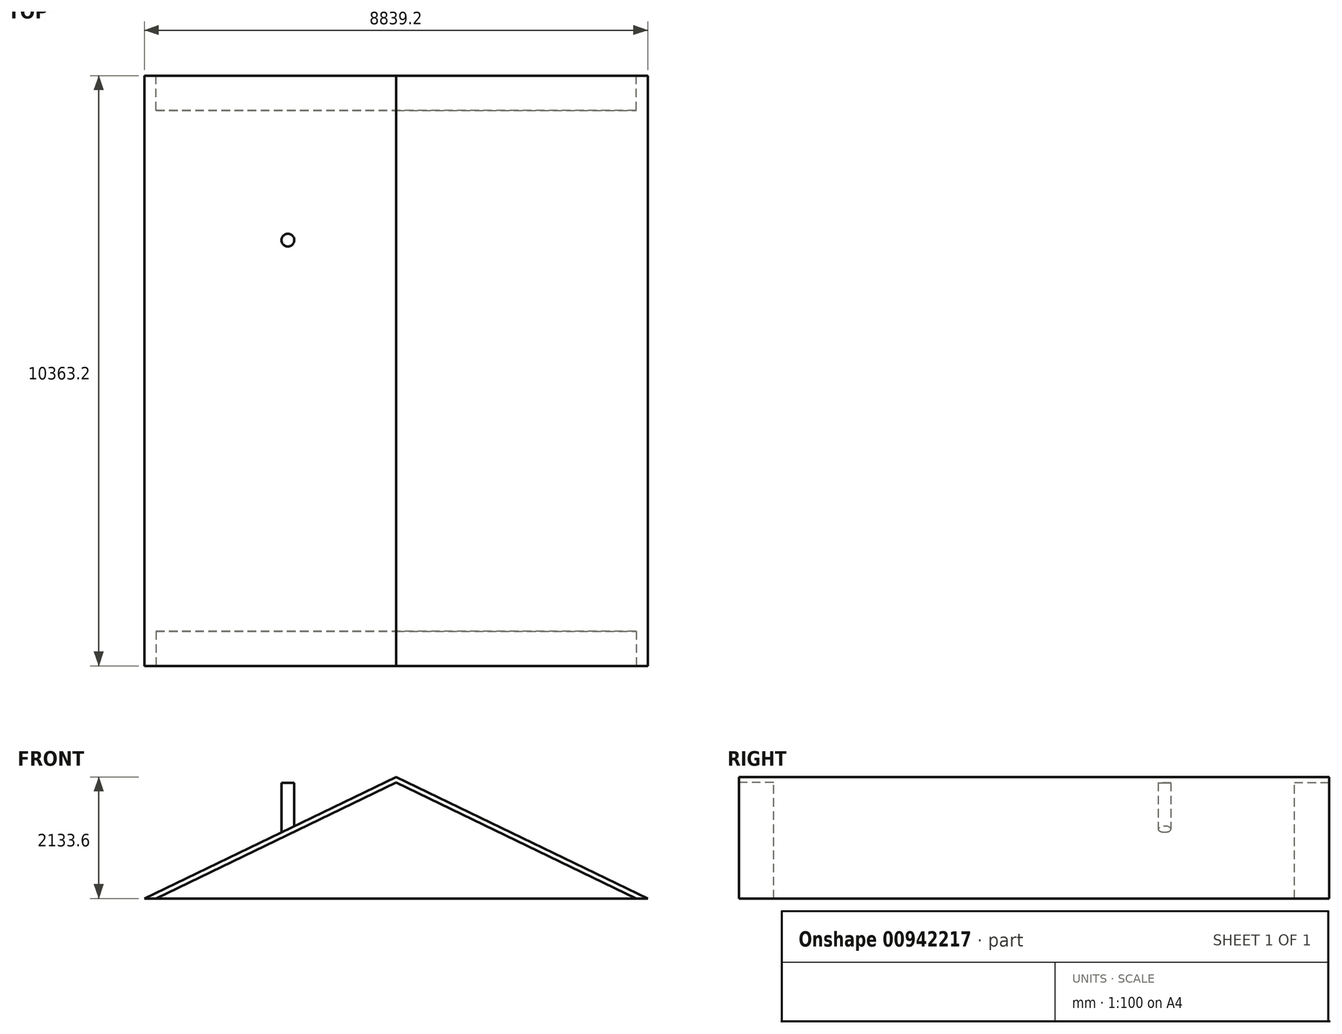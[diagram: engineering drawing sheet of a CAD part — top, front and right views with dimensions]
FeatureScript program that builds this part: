
annotation { "Feature Type Name" : "Feature", "Feature Type Description" : "" }
export const myFeature = defineFeature(function(context is Context, id is Id, definition is map)
    precondition{}
    {
        {
            var Q0;
            Q0=qCreatedBy(makeId("Front.planeOp"),FACE);
            var sketch = newSketch(context, id + "F0", { "sketchPlane" : qUnion([Q0])});
            skLineSegment(sketch, "E0", {"start": v(0, 0) * mm, "end": v(-4419.6, 0) * mm});
            skLineSegment(sketch, "E1", {"start": v(0, 0) * mm, "end": v(4419.6, 0) * mm});
            skLineSegment(sketch, "E2", {"start": v(-4419.6, 0) * mm, "end": v(0, 2133.6) * mm});
            skLineSegment(sketch, "E3", {"start": v(0, 2133.6) * mm, "end": v(4419.6, 0) * mm});
            skPoint(sketch, "E4", {"position": v(-3810, 0) * mm});
            skPoint(sketch, "E5", {"position": v(3810, 0) * mm});
            skSolve(sketch);
        }
        {
            var Q0;
            Q0=makeQuery(id+"F0.imprint","IMPRINT",FACE,{"disambiguationData":[TD([[makeQuery(id+"F0.imprint","IMPRINT",EDGE,{"derivedFrom":sQuery(id+"F0.wireOp",EDGE,"E0")}),-1.0]])]});
            extrude(context, id + "F1", {"entities" : qUnion([Q0]), "oppositeDirection" : true, "depth" : 10363.2 * mm, "offsetDistance" : 25.4 * mm});
        }
        {
            var Q0;
            Q0=makeQuery(id+"F1.opExtrude","CAP_FACE",FACE,{"disambiguationData":[OSD([sQuery(id+"F0.wireOp",EDGE,"E0"),sQuery(id+"F0.wireOp",EDGE,"E1"),sQuery(id+"F0.wireOp",EDGE,"E2"),sQuery(id+"F0.wireOp",EDGE,"E3")])],"isStart":true});
            var sketch = newSketch(context, id + "F2", { "sketchPlane" : qUnion([Q0])});
            skLineSegment(sketch, "E6.0", {"start": v(-4215.11, 0) * mm, "end": v(0, 2034.88) * mm});
            skLineSegment(sketch, "E7.0", {"start": v(0, 2034.88) * mm, "end": v(4215.11, 0) * mm});
            skLineSegment(sketch, "E8", {"start": v(-4419.6, 0) * mm, "end": v(-4215.11, 0) * mm});
            skLineSegment(sketch, "E9", {"start": v(4419.6, 0) * mm, "end": v(4215.11, 0) * mm});
            skSolve(sketch);
        }
        {
            var Q0;
            {var subQ0=sQuery(id+"F2.wireOp",EDGE,"E6.0");Q0=makeQuery(id+"F2.imprint","IMPRINT",FACE,{"disambiguationData":[TD([[makeQuery(id+"F2.imprint","IMPRINT",EDGE,{"derivedFrom":subQ0}),-1.0]])]});}
            extrude(context, id + "F3", {"entities" : qUnion([Q0]), "operationType" : NewBodyOperationType.REMOVE, "oppositeDirection" : true, "depth" : 609.6 * mm, "offsetDistance" : 25.4 * mm});
        }
        {
            var Q0;
            Q0=makeQuery(id+"F1.opExtrude","CAP_FACE",FACE,{"disambiguationData":[OSD([sQuery(id+"F0.wireOp",EDGE,"E0"),sQuery(id+"F0.wireOp",EDGE,"E1"),sQuery(id+"F0.wireOp",EDGE,"E2"),sQuery(id+"F0.wireOp",EDGE,"E3")])],"isStart":false});
            var sketch = newSketch(context, id + "F4", { "sketchPlane" : qUnion([Q0])});
            skLineSegment(sketch, "E10.0", {"start": v(0, 2034.88) * mm, "end": v(-4215.11, 0) * mm});
            skLineSegment(sketch, "E11.0", {"start": v(4215.11, 0) * mm, "end": v(0, 2034.88) * mm});
            skLineSegment(sketch, "E12", {"start": v(-4419.6, 0) * mm, "end": v(-4215.11, 0) * mm});
            skLineSegment(sketch, "E13", {"start": v(4419.6, 0) * mm, "end": v(4215.11, 0) * mm});
            skSolve(sketch);
        }
        {
            var Q0;
            {var subQ0=sQuery(id+"F4.wireOp",EDGE,"E10.0");Q0=makeQuery(id+"F4.imprint","IMPRINT",FACE,{"disambiguationData":[TD([[makeQuery(id+"F4.imprint","IMPRINT",EDGE,{"derivedFrom":subQ0}),1.0]])]});}
            extrude(context, id + "F5", {"entities" : qUnion([Q0]), "operationType" : NewBodyOperationType.REMOVE, "oppositeDirection" : true, "depth" : 609.6 * mm, "offsetDistance" : 25.4 * mm});
        }
        {
            var Q0;
            Q0=makeQuery(id+"F1.opExtrude","SWEPT_FACE",FACE,{"disambiguationData":[OSD([sQuery(id+"F0.wireOp",EDGE,"E0"),sQuery(id+"F0.wireOp",EDGE,"E1")])]});
            var sketch = newSketch(context, id + "F6", { "sketchPlane" : qUnion([Q0])});
            skCircle(sketch, "E14", {"center": v(-1898.52, -7475.07) * mm, "radius": 111.72 * mm});
            skSolve(sketch);
        }
        {
            var Q0;
            Q0=makeQuery(id+"F6.imprint","IMPRINT",FACE,{"disambiguationData":[TD([[makeQuery(id+"F6.imprint","IMPRINT",EDGE,{"derivedFrom":sQuery(id+"F6.wireOp",EDGE,"E14")}),1.0]])]});
            extrude(context, id + "F7", {"entities" : qUnion([Q0]), "operationType" : NewBodyOperationType.ADD, "oppositeDirection" : true, "depth" : 2032 * mm, "offsetDistance" : 25.4 * mm});
        }
    });
